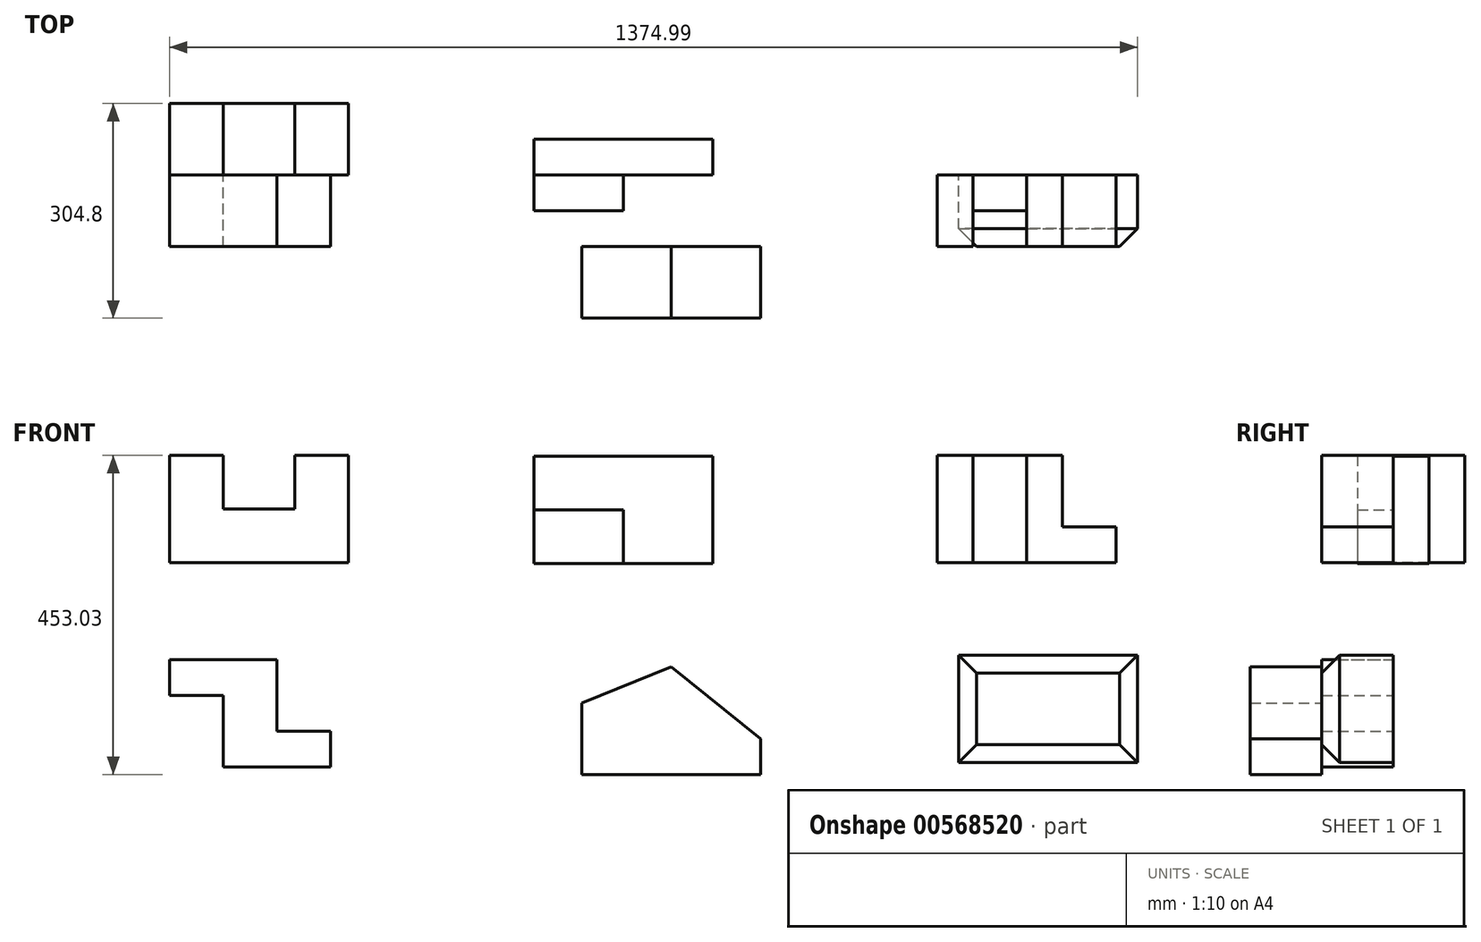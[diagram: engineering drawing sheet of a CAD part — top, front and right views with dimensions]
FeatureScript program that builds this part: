
annotation { "Feature Type Name" : "Feature", "Feature Type Description" : "" }
export const myFeature = defineFeature(function(context is Context, id is Id, definition is map)
    precondition{}
    {
        {
            var Q0;
            Q0=qCreatedBy(makeId("Front.planeOp"),FACE);
            var sketch = newSketch(context, id + "F0", { "sketchPlane" : qUnion([Q0])});
            skLineSegment(sketch, "E0", {"start": v(0, 0) * mm, "end": v(254, 0) * mm});
            skLineSegment(sketch, "E1", {"start": v(254, 0) * mm, "end": v(254, 152.4) * mm});
            skLineSegment(sketch, "E2", {"start": v(254, 152.4) * mm, "end": v(177.8, 152.4) * mm});
            skLineSegment(sketch, "E3", {"start": v(177.8, 152.4) * mm, "end": v(177.8, 76.2) * mm});
            skLineSegment(sketch, "E4", {"start": v(177.8, 76.2) * mm, "end": v(76.2, 76.2) * mm});
            skLineSegment(sketch, "E5", {"start": v(76.2, 76.2) * mm, "end": v(76.2, 152.4) * mm});
            skLineSegment(sketch, "E6", {"start": v(76.2, 152.4) * mm, "end": v(0, 152.4) * mm});
            skLineSegment(sketch, "E7", {"start": v(0, 152.4) * mm, "end": v(0, 0) * mm});
            skSolve(sketch);
        }
        {
            var Q0;
            Q0=makeQuery(id+"F0.imprint","IMPRINT",FACE,{"disambiguationData":[TD([[makeQuery(id+"F0.imprint","IMPRINT",EDGE,{"derivedFrom":sQuery(id+"F0.wireOp",EDGE,"E0")}),1.0]])]});
            extrude(context, id + "F1", {"entities" : qUnion([Q0]), "oppositeDirection" : true, "depth" : 101.6 * mm, "offsetDistance" : 25.4 * mm});
        }
        {
            var Q0;
            Q0=qCreatedBy(makeId("Front.planeOp"),FACE);
            var sketch = newSketch(context, id + "F2", { "sketchPlane" : qUnion([Q0])});
            skLineSegment(sketch, "E8.bottom", {"start": v(517.43, 151.4) * mm, "end": v(771.43, 151.4) * mm});
            skLineSegment(sketch, "E8.top", {"start": v(517.43, -1) * mm, "end": v(771.43, -1) * mm});
            skLineSegment(sketch, "E8.left", {"start": v(517.43, 151.4) * mm, "end": v(517.43, -1) * mm});
            skLineSegment(sketch, "E8.right", {"start": v(771.43, 151.4) * mm, "end": v(771.43, -1) * mm});
            skLineSegment(sketch, "E9", {"start": v(517.43, 75.2) * mm, "end": v(644.43, 75.2) * mm});
            skLineSegment(sketch, "E10", {"start": v(644.43, 75.2) * mm, "end": v(644.43, -1) * mm});
            skSolve(sketch);
        }
        {
            var Q0;
            {var subQ4=sQuery(id+"F2.wireOp",EDGE,"E9");Q0=makeQuery(id+"F2.imprint","IMPRINT",FACE,{"disambiguationData":[TD([[makeQuery(id+"F2.imprint","IMPRINT",EDGE,{"derivedFrom":subQ4}),-1.0]])]});}
            var Q1;
            Q1 = qSketchRegion(id + "F4", true);
            extrude(context, id + "F3", {"entities" : qUnion([Q0, Q1]), "depth" : 50.8 * mm, "offsetDistance" : 25.4 * mm});
        }
        {
            var Q0;
            Q0=makeQuery(id+"F3.opExtrude","CAP_FACE",FACE,{"disambiguationData":[OSD([sQuery(id+"F2.wireOp",EDGE,"E8.top"),sQuery(id+"F2.wireOp",EDGE,"E8.left"),sQuery(id+"F2.wireOp",EDGE,"E9"),sQuery(id+"F2.wireOp",EDGE,"E10")])],"isStart":true});
            var sketch = newSketch(context, id + "F4", { "sketchPlane" : qUnion([Q0])});
            skLineSegment(sketch, "E11.bottom", {"start": v(-517.43, -1) * mm, "end": v(-771.43, -1) * mm});
            skLineSegment(sketch, "E11.top", {"start": v(-517.43, 151.4) * mm, "end": v(-771.43, 151.4) * mm});
            skLineSegment(sketch, "E11.left", {"start": v(-517.43, -1) * mm, "end": v(-517.43, 151.4) * mm});
            skLineSegment(sketch, "E11.right", {"start": v(-771.43, -1) * mm, "end": v(-771.43, 151.4) * mm});
            skSolve(sketch);
        }
        {
            var Q0;
            {var subQ4=makeQuery(id+"F3.opExtrude","CAP_EDGE",EDGE,{"disambiguationData":[OSD([sQuery(id+"F2.wireOp",EDGE,"E9")])],"isStart":true});Q0=makeQuery(id+"F4.imprint","IMPRINT",FACE,{"disambiguationData":[TD([[makeQuery(id+"F4.imprint","IMPRINT",EDGE,{"derivedFrom":subQ4}),1.0]])]});}
            var Q1;
            {var subQ3=sQuery(id+"F4.wireOp",EDGE,"E11.top");Q1=makeQuery(id+"F4.imprint","IMPRINT",FACE,{"disambiguationData":[TD([[makeQuery(id+"F4.imprint","IMPRINT",EDGE,{"derivedFrom":subQ3}),1.0]])]});}
            extrude(context, id + "F5", {"entities" : qUnion([Q0, Q1]), "operationType" : NewBodyOperationType.ADD, "depth" : 50.8 * mm, "offsetDistance" : 25.4 * mm});
        }
        {
            var Q0;
            Q0=makeQuery(id+"F5.opExtrude","CAP_FACE",FACE,{"disambiguationData":[OSD([sQuery(id+"F4.wireOp",EDGE,"E11.bottom"),sQuery(id+"F4.wireOp",EDGE,"E11.top"),sQuery(id+"F4.wireOp",EDGE,"E11.left"),sQuery(id+"F4.wireOp",EDGE,"E11.right")])],"isStart":true});
            var sketch = newSketch(context, id + "F6", { "sketchPlane" : qUnion([Q0])});
            skLineSegment(sketch, "E12", {"start": v(1090.55, 152.4) * mm, "end": v(1090.55, 0) * mm});
            skLineSegment(sketch, "E13", {"start": v(1090.55, 0) * mm, "end": v(1344.55, 0) * mm});
            skLineSegment(sketch, "E14", {"start": v(1344.55, 0) * mm, "end": v(1344.55, 50.8) * mm});
            skLineSegment(sketch, "E15", {"start": v(1344.55, 50.8) * mm, "end": v(1268.35, 50.8) * mm});
            skLineSegment(sketch, "E16", {"start": v(1268.35, 50.8) * mm, "end": v(1268.35, 152.4) * mm});
            skLineSegment(sketch, "E17", {"start": v(1268.35, 152.4) * mm, "end": v(1090.55, 152.4) * mm});
            skLineSegment(sketch, "E18", {"start": v(1141.35, 152.4) * mm, "end": v(1141.35, 0) * mm});
            skLineSegment(sketch, "E19", {"start": v(1217.55, 152.4) * mm, "end": v(1217.55, 0) * mm});
            skSolve(sketch);
        }
        {
            var Q0;
            {var subQ1=sQuery(id+"F6.wireOp",EDGE,"E14");Q0=makeQuery(id+"F6.imprint","IMPRINT",FACE,{"disambiguationData":[TD([[makeQuery(id+"F6.imprint","IMPRINT",EDGE,{"derivedFrom":subQ1}),1.0]])]});}
            var Q1;
            {var subQ0=sQuery(id+"F6.wireOp",EDGE,"E12");Q1=makeQuery(id+"F6.imprint","IMPRINT",FACE,{"disambiguationData":[TD([[makeQuery(id+"F6.imprint","IMPRINT",EDGE,{"derivedFrom":subQ0}),1.0]])]});}
            extrude(context, id + "F7", {"entities" : qUnion([Q0, Q1]), "depth" : 101.6 * mm, "offsetDistance" : 25.4 * mm});
        }
        {
            var Q0;
            Q0=makeQuery(id+"F7.opExtrude","CAP_FACE",FACE,{"disambiguationData":[OSD([sQuery(id+"F6.wireOp",EDGE,"E13"),sQuery(id+"F6.wireOp",EDGE,"E14"),sQuery(id+"F6.wireOp",EDGE,"E15"),sQuery(id+"F6.wireOp",EDGE,"E16"),sQuery(id+"F6.wireOp",EDGE,"E17"),sQuery(id+"F6.wireOp",EDGE,"E19")])],"isStart":true});
            var sketch = newSketch(context, id + "F8", { "sketchPlane" : qUnion([Q0])});
            skLineSegment(sketch, "E20.bottom", {"start": v(-1217.55, 152.4) * mm, "end": v(-1141.35, 152.4) * mm});
            skLineSegment(sketch, "E20.top", {"start": v(-1217.55, 0) * mm, "end": v(-1141.35, 0) * mm});
            skLineSegment(sketch, "E20.left", {"start": v(-1217.55, 152.4) * mm, "end": v(-1217.55, 0) * mm});
            skLineSegment(sketch, "E20.right", {"start": v(-1141.35, 152.4) * mm, "end": v(-1141.35, 0) * mm});
            skSolve(sketch);
        }
        {
            var Q0;
            Q0 = qSketchRegion(id + "F8", true);
            extrude(context, id + "F9", {"entities" : qUnion([Q0]), "oppositeDirection" : true, "depth" : 50.8 * mm, "offsetDistance" : 25.4 * mm});
        }
        {
            var Q0;
            Q0=makeQuery(id+"F1.opExtrude","CAP_FACE",FACE,{"disambiguationData":[OSD([sQuery(id+"F0.wireOp",EDGE,"E0"),sQuery(id+"F0.wireOp",EDGE,"E1"),sQuery(id+"F0.wireOp",EDGE,"E2"),sQuery(id+"F0.wireOp",EDGE,"E3"),sQuery(id+"F0.wireOp",EDGE,"E4"),sQuery(id+"F0.wireOp",EDGE,"E5"),sQuery(id+"F0.wireOp",EDGE,"E6"),sQuery(id+"F0.wireOp",EDGE,"E7")])],"isStart":true});
            var sketch = newSketch(context, id + "F10", { "sketchPlane" : qUnion([Q0])});
            skLineSegment(sketch, "E21", {"start": v(0, -137.76) * mm, "end": v(152.4, -137.76) * mm});
            skLineSegment(sketch, "E22", {"start": v(152.4, -137.76) * mm, "end": v(152.4, -239.36) * mm});
            skLineSegment(sketch, "E23", {"start": v(152.4, -239.36) * mm, "end": v(228.6, -239.36) * mm});
            skLineSegment(sketch, "E24", {"start": v(228.6, -239.36) * mm, "end": v(228.6, -290.16) * mm});
            skLineSegment(sketch, "E25", {"start": v(228.6, -290.16) * mm, "end": v(76.2, -290.16) * mm});
            skLineSegment(sketch, "E26", {"start": v(76.2, -290.16) * mm, "end": v(76.2, -188.56) * mm});
            skLineSegment(sketch, "E27", {"start": v(76.2, -188.56) * mm, "end": v(0, -188.56) * mm});
            skLineSegment(sketch, "E28", {"start": v(0, -188.56) * mm, "end": v(0, -137.76) * mm});
            skSolve(sketch);
        }
        {
            var Q0;
            Q0=makeQuery(id+"F10.imprint","IMPRINT",FACE,{"disambiguationData":[TD([[makeQuery(id+"F10.imprint","IMPRINT",EDGE,{"derivedFrom":sQuery(id+"F10.wireOp",EDGE,"E21")}),-1.0]])]});
            extrude(context, id + "F11", {"entities" : qUnion([Q0]), "depth" : 101.6 * mm, "offsetDistance" : 25.4 * mm});
        }
        {
            var Q0;
            Q0=makeQuery(id+"F11.opExtrude","CAP_FACE",FACE,{"disambiguationData":[OSD([sQuery(id+"F10.wireOp",EDGE,"E21"),sQuery(id+"F10.wireOp",EDGE,"E22"),sQuery(id+"F10.wireOp",EDGE,"E23"),sQuery(id+"F10.wireOp",EDGE,"E24"),sQuery(id+"F10.wireOp",EDGE,"E25"),sQuery(id+"F10.wireOp",EDGE,"E26"),sQuery(id+"F10.wireOp",EDGE,"E27"),sQuery(id+"F10.wireOp",EDGE,"E28")])],"isStart":false});
            var sketch = newSketch(context, id + "F12", { "sketchPlane" : qUnion([Q0])});
            skLineSegment(sketch, "E29", {"start": v(585.47, -300.63) * mm, "end": v(585.47, -199.03) * mm});
            skLineSegment(sketch, "E30", {"start": v(585.47, -199.03) * mm, "end": v(712.47, -148.04) * mm});
            skLineSegment(sketch, "E31", {"start": v(712.47, -148.04) * mm, "end": v(839.47, -249.83) * mm});
            skLineSegment(sketch, "E32", {"start": v(839.47, -249.83) * mm, "end": v(839.47, -300.63) * mm});
            skLineSegment(sketch, "E33", {"start": v(585.47, -300.63) * mm, "end": v(839.47, -300.63) * mm});
            skSolve(sketch);
        }
        {
            var Q0;
            Q0=makeQuery(id+"F5.opExtrude","CAP_FACE",FACE,{"disambiguationData":[OSD([sQuery(id+"F4.wireOp",EDGE,"E11.bottom"),sQuery(id+"F4.wireOp",EDGE,"E11.top"),sQuery(id+"F4.wireOp",EDGE,"E11.left"),sQuery(id+"F4.wireOp",EDGE,"E11.right")])],"isStart":true});
            var sketch = newSketch(context, id + "F13", { "sketchPlane" : qUnion([Q0])});
            skLineSegment(sketch, "E34.bottom", {"start": v(1120.99, -131) * mm, "end": v(1374.99, -131) * mm});
            skLineSegment(sketch, "E34.top", {"start": v(1120.99, -283.4) * mm, "end": v(1374.99, -283.4) * mm});
            skLineSegment(sketch, "E34.left", {"start": v(1120.99, -131) * mm, "end": v(1120.99, -283.4) * mm});
            skLineSegment(sketch, "E34.right", {"start": v(1374.99, -131) * mm, "end": v(1374.99, -283.4) * mm});
            skSolve(sketch);
        }
        {
            var Q0;
            Q0=makeQuery(id+"F13.imprint","IMPRINT",FACE,{"disambiguationData":[TD([[makeQuery(id+"F13.imprint","IMPRINT",EDGE,{"derivedFrom":sQuery(id+"F13.wireOp",EDGE,"E34.bottom")}),-1.0]])]});
            extrude(context, id + "F14", {"entities" : qUnion([Q0]), "depth" : 101.6 * mm, "offsetDistance" : 25.4 * mm});
        }
        {
            var Q0;
            Q0 = qSketchRegion(id + "F12", true);
            extrude(context, id + "F15", {"entities" : qUnion([Q0]), "depth" : 101.6 * mm, "offsetDistance" : 25.4 * mm});
        }
        {
            var Q0;
            Q0=makeQuery(id+"F14.opExtrude","CAP_EDGE",EDGE,{"disambiguationData":[OSD([sQuery(id+"F13.wireOp",EDGE,"E34.bottom")])],"isStart":false});
            var Q1;
            Q1=makeQuery(id+"F14.opExtrude","CAP_EDGE",EDGE,{"disambiguationData":[OSD([sQuery(id+"F13.wireOp",EDGE,"E34.right")])],"isStart":false});
            var Q2;
            Q2=makeQuery(id+"F14.opExtrude","CAP_EDGE",EDGE,{"disambiguationData":[OSD([sQuery(id+"F13.wireOp",EDGE,"E34.top")])],"isStart":false});
            var Q3;
            Q3=makeQuery(id+"F14.opExtrude","CAP_EDGE",EDGE,{"disambiguationData":[OSD([sQuery(id+"F13.wireOp",EDGE,"E34.left")])],"isStart":false});
            chamfer(context, id + "F16", {"entities" : qUnion([Q0, Q1, Q2, Q3]), "width" : 25.4 * mm, "tangentPropagation" : true});
        }
    });
